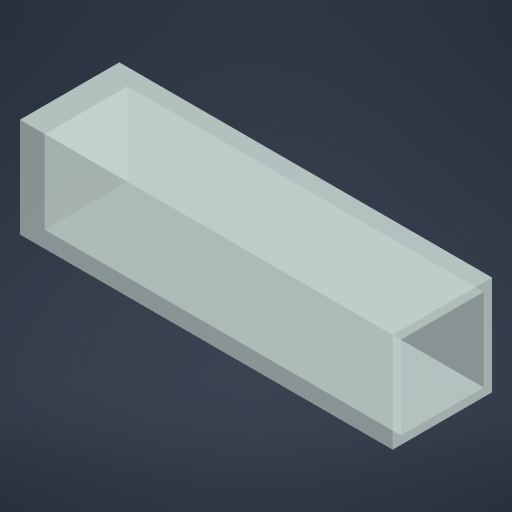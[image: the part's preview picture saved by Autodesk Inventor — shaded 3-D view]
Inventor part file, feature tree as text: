
AUTODESK INVENTOR PART (.ipt)
format: ipt  version: 2024.1 (Build 281209000, 209)  size: 167,936 bytes
history: native  units: mm
features: extrude x2, sketch x2
ambient origin geometry x8: Origin, YZ Plane, XZ Plane, XY Plane, X Axis, Y Axis, Z Axis, Center Point
bodies: Solid1 (feature_tree)
feature tree (4):
  extrude  "Extrusion1"  Depth=12.0mm
  extrude  "Extrusion2"  Depth=10.0mm
  sketch  "Sketch1"  dims[d0=12.0mm d1=12.0mm]
  sketch  "Sketch2"  dims[d2=45.0mm d3=0.0mm d4=10.0mm d5=10.0mm d6=43.0mm d7=0.0mm]
